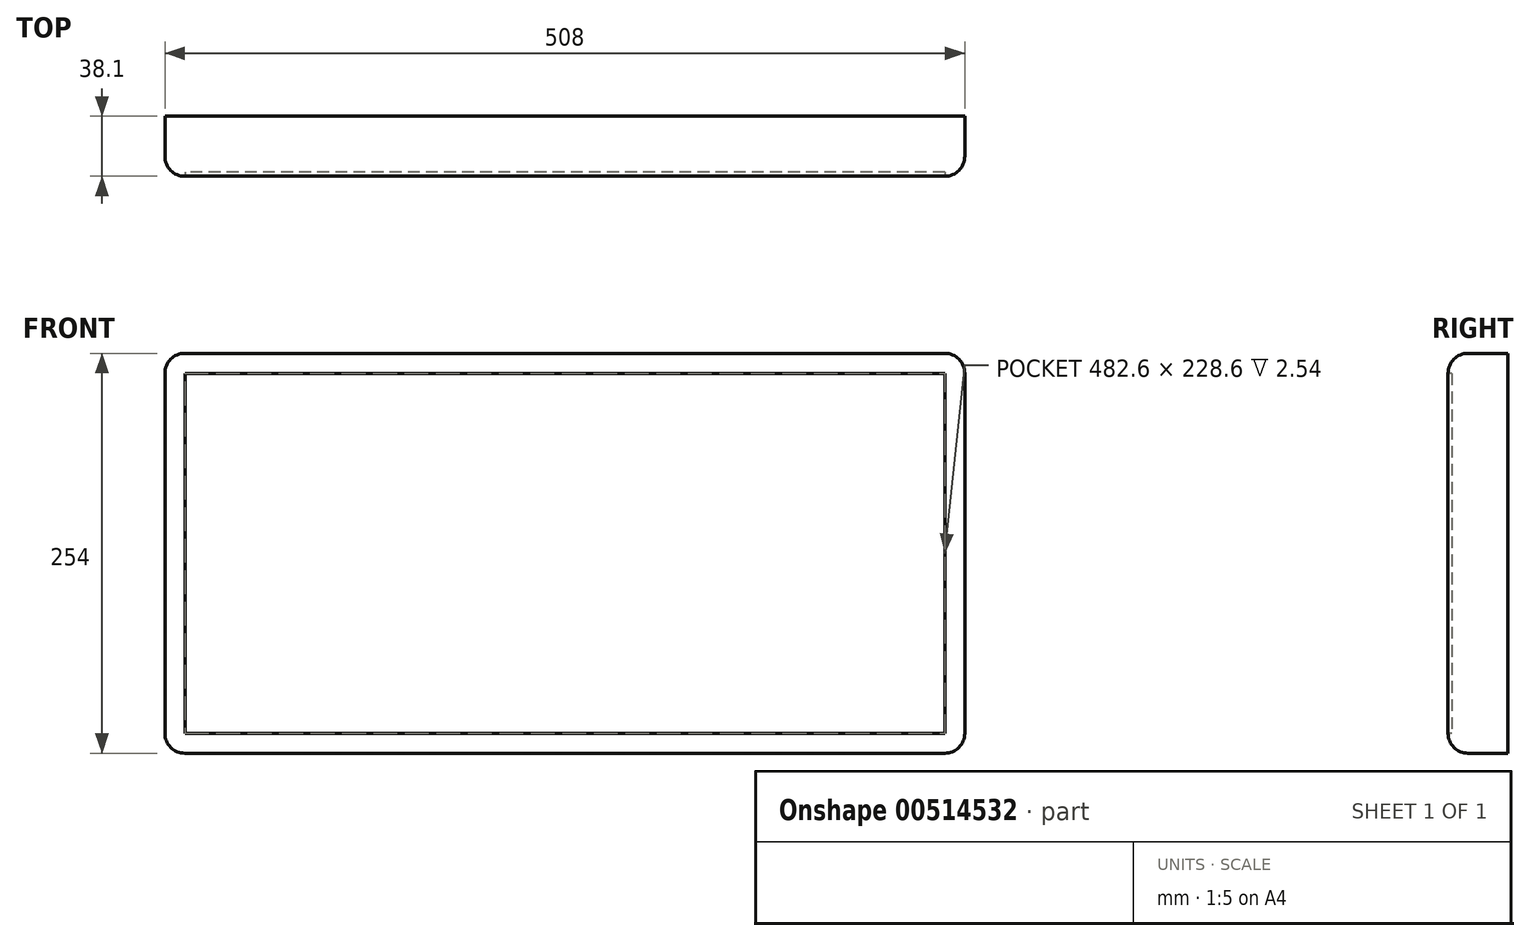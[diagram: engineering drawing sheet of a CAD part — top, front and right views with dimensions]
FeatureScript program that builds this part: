
annotation { "Feature Type Name" : "Feature", "Feature Type Description" : "" }
export const myFeature = defineFeature(function(context is Context, id is Id, definition is map)
    precondition{}
    {
        {
            var Q0;
            Q0=qCreatedBy(makeId("Front.planeOp"),FACE);
            var sketch = newSketch(context, id + "F0", { "sketchPlane" : qUnion([Q0])});
            skLineSegment(sketch, "E0.bottom", {"start": v(254, 127) * mm, "end": v(-254, 127) * mm});
            skLineSegment(sketch, "E0.top", {"start": v(254, -127) * mm, "end": v(-254, -127) * mm});
            skLineSegment(sketch, "E0.left", {"start": v(254, 127) * mm, "end": v(254, -127) * mm});
            skLineSegment(sketch, "E0.right", {"start": v(-254, 127) * mm, "end": v(-254, -127) * mm});
            skPoint(sketch, "E0.middle", {"position": v(0, 0) * mm});
            skSolve(sketch);
        }
        {
            var Q0;
            Q0=makeQuery(id+"F0.imprint","IMPRINT",FACE,{"disambiguationData":[TD([[makeQuery(id+"F0.imprint","IMPRINT",EDGE,{"derivedFrom":sQuery(id+"F0.wireOp",EDGE,"E0.bottom")}),1.0]])]});
            extrude(context, id + "F1", {"entities" : qUnion([Q0]), "depth" : 38.1 * mm, "offsetDistance" : 25.4 * mm});
        }
        {
            var Q0;
            Q0=makeQuery(id+"F1.opExtrude","CAP_FACE",FACE,{"disambiguationData":[OSD([sQuery(id+"F0.wireOp",EDGE,"E0.bottom"),sQuery(id+"F0.wireOp",EDGE,"E0.top"),sQuery(id+"F0.wireOp",EDGE,"E0.left"),sQuery(id+"F0.wireOp",EDGE,"E0.right")])],"isStart":false});
            var Q1;
            Q1=makeQuery(id+"F1.opExtrude","SWEPT_EDGE",EDGE,{"disambiguationData":[OSD([sQuery(id+"F0.wireOp",EDGE,"E0.bottom"),sQuery(id+"F0.wireOp",EDGE,"E0.right")])]});
            var Q2;
            Q2=makeQuery(id+"F1.opExtrude","SWEPT_EDGE",EDGE,{"disambiguationData":[OSD([sQuery(id+"F0.wireOp",EDGE,"E0.bottom"),sQuery(id+"F0.wireOp",EDGE,"E0.left")])]});
            var Q3;
            Q3=makeQuery(id+"F1.opExtrude","SWEPT_EDGE",EDGE,{"disambiguationData":[OSD([sQuery(id+"F0.wireOp",EDGE,"E0.top"),sQuery(id+"F0.wireOp",EDGE,"E0.left")])]});
            var Q4;
            Q4=makeQuery(id+"F1.opExtrude","SWEPT_EDGE",EDGE,{"disambiguationData":[OSD([sQuery(id+"F0.wireOp",EDGE,"E0.top"),sQuery(id+"F0.wireOp",EDGE,"E0.right")])]});
            fillet(context, id + "F2", {"entities" : qUnion([Q0, Q1, Q2, Q3, Q4]), "radius" : 12.7 * mm, "tangentPropagation" : true, "allowEdgeOverflow" : false});
        }
        {
            var Q0;
            Q0=makeQuery(id+"F1.opExtrude","CAP_FACE",FACE,{"disambiguationData":[OSD([sQuery(id+"F0.wireOp",EDGE,"E0.bottom"),sQuery(id+"F0.wireOp",EDGE,"E0.top"),sQuery(id+"F0.wireOp",EDGE,"E0.left"),sQuery(id+"F0.wireOp",EDGE,"E0.right")])],"isStart":false});
            extrude(context, id + "F3", {"entities" : qUnion([Q0]), "operationType" : NewBodyOperationType.REMOVE, "oppositeDirection" : true, "depth" : 2.54 * mm, "offsetDistance" : 25.4 * mm});
        }
    });
